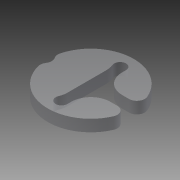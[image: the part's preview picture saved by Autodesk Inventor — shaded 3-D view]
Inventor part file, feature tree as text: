
AUTODESK INVENTOR PART (.ipt)
format: ipt  version: 2013 (Build 170138000, 138)  size: 114,688 bytes
history: native  units: mm
features: extrude x1
ambient origin geometry x8: Origin, YZ Plane, XZ Plane, XY Plane, X Axis, Y Axis, Z Axis, Center Point
feature tree (1):
  extrude  "Extrusion2"  Depth=22.0mm
